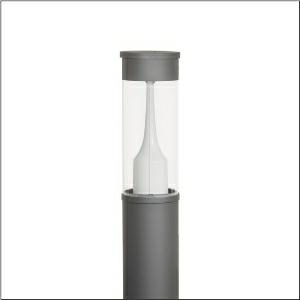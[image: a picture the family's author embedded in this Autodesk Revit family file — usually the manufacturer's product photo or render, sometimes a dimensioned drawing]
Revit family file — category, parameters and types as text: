
# Revit family: city-light_260_iq___st1_2a_5xa5295af14h_a960
name_source: partatom
category: Lighting Fixtures
units: mm (PartAtom-declared; Revit-internal decimal feet)

## family parameters
Cut with Voids When Loaded = No
Host = Face
Light Source = No
Part Type = Normal
Room Calculation Point = No
Round Connector Dimension = Use Diameter
Shared = No

## types (1)
- --- (1 x LED, 1540 lm, 12.9 W, 2200K)
    Apparent Load = 13 VA
    CIE Flux Codes = 22 61 93 96 100
    Color Rendering = 70
    Color Temperature = 2200K
    Default Elevation = 1800 mm
    Description = City-Light 260 iQ, light pillar, Module 540 iQ-SR, primary light control with 3 zone facetted reflector, of plastic, silver coated, highly specular, structured, primary optical cover: cover, of PMMA, transparent, partly coated, light distribution: ST1.2a, primary light characteristic: asymmetric, LED, High Power LED, rated luminous flux: 1.540lm, luminous efficacy: 119lm/W, light colour: 722, colour temperature: 2200K, control gear: ECG iQ, control: presetting dimming logarithmic, Street-Remote, Auto-Match, Temp-Guard, Lumen-Switch, Night-Set, Smart-Wire, Light-Fading, Desk-Remote (wireless, voltage-free reading and setting of iQ features in the workshop via application-optimized NFC function/RFID function), optimised constant luminous flux control (CLO 2.0), with terminal, 6-pole, max. 2.5mm², mains connection: 220..240V, AC, 50/60Hz, start of lifetime: 13W, end of lifetime: 13W, reduction: 6W, luminaire housing, cylindrical, of extruded aluminium section, coated, Siteco® metallic grey (DB 702S), length: 2.600mm, diameter: 200mm, Module 540 iQ-SR, traffic white (RAL 9016), equipment: standard, protection rating (complete): IP65, insulation class (complete): insulation class II (safety insulation), certification: CE, ENEC, VDE, packaging unit: 1 piece

Light Distribution: ST1.2a
    Height = 500 mm
    Lamp = 1 x LED
    Lamp Light Flux = 1540 lm
    Lamp Power = 12.9 W
    Lamp count = 1
    Length = 200 mm  [stored 0.656168 ft]
    Luminous efficacy = 119 lm/W
    Manufacturer = Siteco
    ModVariant = No
    Model = 5XA5295AF14H
    Number of Poles = 1
    OnlyDefault = Yes
    Power Factor = 1
    Product Name = City-Light 260 iQ | ST1.2a
    Product group = light pillar | pylon top
    ProductGroupID = 6103
    Protection Class = Protection class II
    Protection Degree = IP 65
    RLX_Detail_Level = 1
    RlxData = <blob elided: 61205 chars, md5=d2457972>
    Socket = socket
    Standby Power = 0 W
    System Light Flux = 1540 lm
    System Power = 13 W
    Type Comments = factory setting: luminous flux: 100 % | dim-lin: 254 | 516 mA
    Type Image = l_1006918.jpg
    URL = http://relux.com
    VarID = @adj_070481
    Voltage = 0 V
    Weight = 0.00 kg
    Width = 0 mm  [stored 0 ft]

note: [stored X ft] marks values corroborated as IEEE doubles in the binary element streams (Revit-internal decimal feet)

## geometry (parser evidence)
native form markers: Blend x4, Sweep x11
no freeform markers — native parametric forms only
